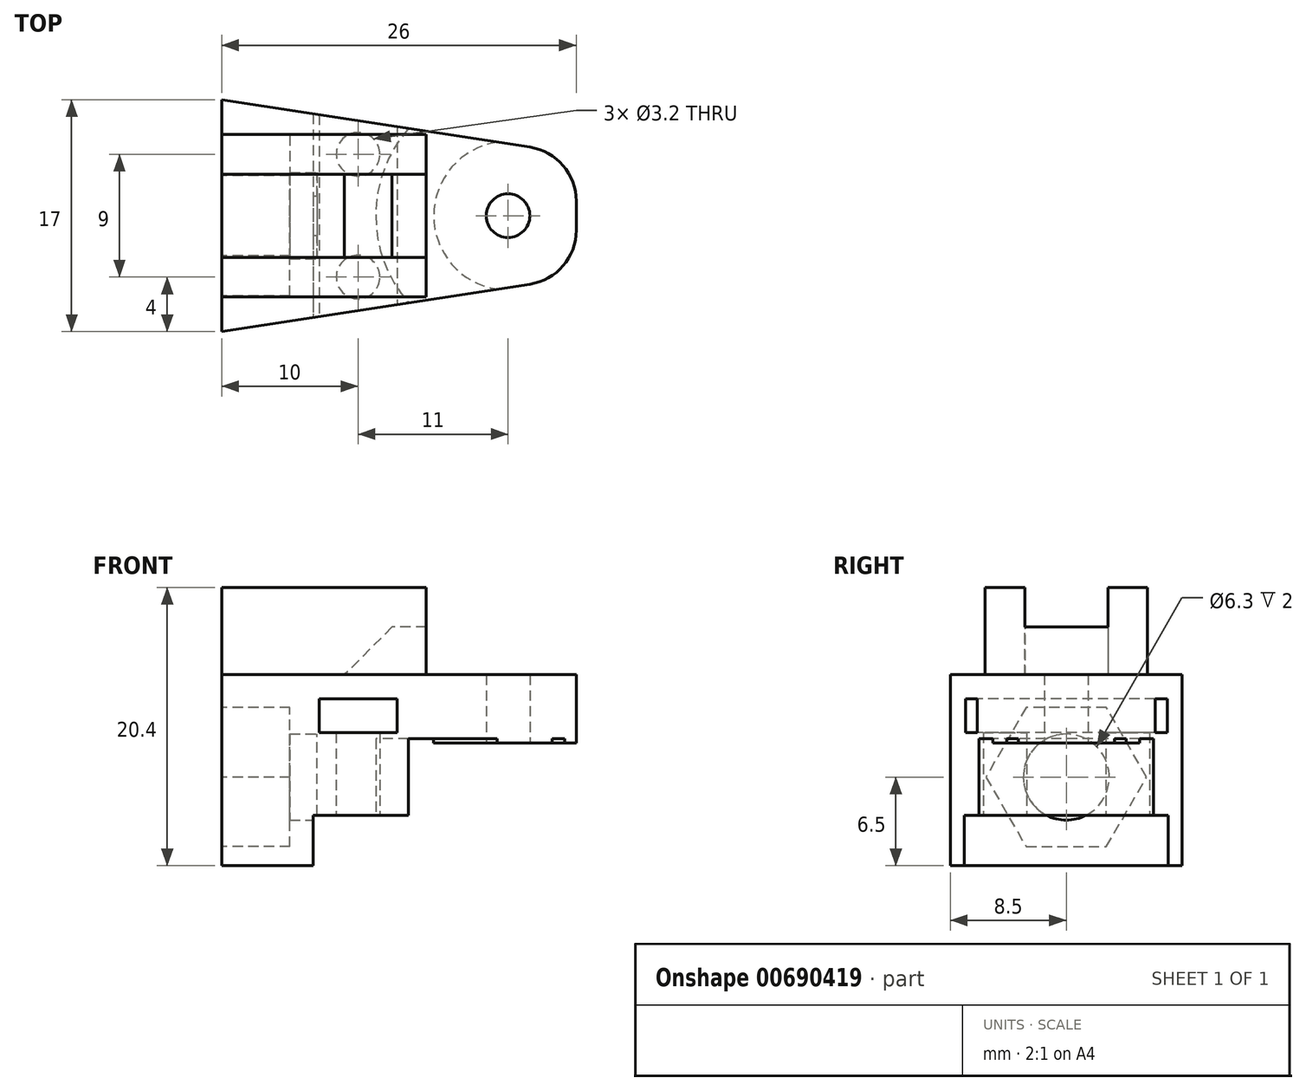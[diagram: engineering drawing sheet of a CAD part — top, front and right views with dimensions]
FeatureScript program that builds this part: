
annotation { "Feature Type Name" : "Feature", "Feature Type Description" : "" }
export const myFeature = defineFeature(function(context is Context, id is Id, definition is map)
    precondition{}
    {
        {
            var Q0;
            Q0=qCreatedBy(makeId("Top.planeOp"),FACE);
            var sketch = newSketch(context, id + "F0", { "sketchPlane" : qUnion([Q0])});
            skLineSegment(sketch, "E0.bottom", {"start": v(1.6, -5.02) * mm, "end": v(-21, -8.5) * mm});
            skLineSegment(sketch, "E0.top", {"start": v(1.6, 5.02) * mm, "end": v(-21, 8.5) * mm});
            skLineSegment(sketch, "E0.left", {"start": v(5, -1.07) * mm, "end": v(5, 1.07) * mm});
            skLineSegment(sketch, "E0.right", {"start": v(-21, -8.5) * mm, "end": v(-21, 8.5) * mm});
            skLineSegment(sketch, "E1", {"start": v(5, 0) * mm, "end": v(-21, 0) * mm, "construction": true});
            skPoint(sketch, "E2.visualSharp", {"position": v(5, -4.5) * mm});
            skArc(sketch, "E2.filletArc", {"start": v(1.6, -5.02) * mm, "mid": v(4.04, -3.67) * mm, "end": v(5, -1.07) * mm});
            skPoint(sketch, "E3.visualSharp", {"position": v(5, 4.5) * mm});
            skArc(sketch, "E3.filletArc", {"start": v(5, 1.07) * mm, "mid": v(4.04, 3.67) * mm, "end": v(1.6, 5.02) * mm});
            skSolve(sketch);
        }
        {
            var Q0;
            Q0=qSketchRegion(id+"F0",true);
            extrude(context, id + "F1", {"entities" : qUnion([Q0]), "depth" : 8 * mm, "offsetDistance" : 25 * mm, "hasSecondDirection" : true, "secondDirectionOppositeDirection" : true, "secondDirectionDepth" : 6 * mm});
        }
        {
            var Q0;
            Q0=qCreatedBy(makeId("Top.planeOp"),FACE);
            var sketch = newSketch(context, id + "F2", { "sketchPlane" : qUnion([Q0])});
            skCircle(sketch, "E4", {"center": v(0, 0) * mm, "radius": 8.3 * mm});
            skCircle(sketch, "E5", {"center": v(0, 0) * mm, "radius": 2.95 * mm});
            skSolve(sketch);
        }
        {
            var Q0;
            Q0=qSketchRegion(id+"F2",true);
            extrude(context, id + "F3", {"entities" : qUnion([Q0]), "operationType" : NewBodyOperationType.REMOVE, "oppositeDirection" : true, "depth" : 3 * mm, "offsetDistance" : 25 * mm, "hasSecondDirection" : true, "secondDirectionOppositeDirection" : false, "secondDirectionDepth" : 3 * mm});
        }
        {
            var Q0;
            Q0=qCreatedBy(makeId("Top.planeOp"),FACE);
            var sketch = newSketch(context, id + "F4", { "sketchPlane" : qUnion([Q0])});
            skArc(sketch, "E6", {"start": v(5, 2.17) * mm, "mid": v(-5.45, 0) * mm, "end": v(5, -2.17) * mm});
            skArc(sketch, "E7", {"start": v(5, 8.31) * mm, "mid": v(-9.7, 0) * mm, "end": v(5, -8.31) * mm});
            skLineSegment(sketch, "E8", {"start": v(5, 8.31) * mm, "end": v(5, 2.17) * mm});
            skLineSegment(sketch, "E9.trimOffspring", {"start": v(5, -2.17) * mm, "end": v(5, -8.31) * mm});
            skSolve(sketch);
        }
        {
            var Q0;
            Q0=qSketchRegion(id+"F4",true);
            extrude(context, id + "F5", {"entities" : qUnion([Q0]), "operationType" : NewBodyOperationType.REMOVE, "depth" : 3.3 * mm, "offsetDistance" : 25 * mm, "hasSecondDirection" : true, "secondDirectionOppositeDirection" : true, "secondDirectionDepth" : 3.3 * mm});
        }
        {
            var Q0;
            Q0=qCreatedBy(makeId("Right.planeOp"),FACE);
            var sketch = newSketch(context, id + "F6", { "sketchPlane" : qUnion([Q0])});
            skPoint(sketch, "E10", {"position": v(0, 0) * mm});
            skCircle(sketch, "E11", {"center": v(0, 0.5) * mm, "radius": 3.15 * mm});
            skSolve(sketch);
        }
        {
            var Q0;
            Q0=qSketchRegion(id+"F6",true);
            extrude(context, id + "F7", {"entities" : qUnion([Q0]), "operationType" : NewBodyOperationType.REMOVE, "oppositeDirection" : true, "depth" : 40 * mm, "offsetDistance" : 25 * mm, "hasSecondDirection" : true, "secondDirectionOppositeDirection" : true, "secondDirectionDepth" : 14 * mm});
        }
        {
            var Q0;
            Q0=makeQuery(id+"F1.opExtrude","SWEPT_FACE",FACE,{"disambiguationData":[OSD([sQuery(id+"F0.wireOp",EDGE,"E0.right")])]});
            var sketch = newSketch(context, id + "F8", { "sketchPlane" : qUnion([Q0])});
            skCircle(sketch, "E12.cCircle", {"center": v(0, 0.5) * mm, "radius": 5.1 * mm, "construction": true});
            skLineSegment(sketch, "E12.0", {"start": v(-2.94, 5.6) * mm, "end": v(2.94, 5.6) * mm});
            skLineSegment(sketch, "E12.1", {"start": v(2.94, 5.6) * mm, "end": v(5.89, 0.5) * mm});
            skLineSegment(sketch, "E12.2", {"start": v(5.89, 0.5) * mm, "end": v(2.94, -4.6) * mm});
            skLineSegment(sketch, "E12.3", {"start": v(2.94, -4.6) * mm, "end": v(-2.94, -4.6) * mm});
            skLineSegment(sketch, "E12.4", {"start": v(-2.94, -4.6) * mm, "end": v(-5.89, 0.5) * mm});
            skLineSegment(sketch, "E12.5", {"start": v(-5.89, 0.5) * mm, "end": v(-2.94, 5.6) * mm});
            skSolve(sketch);
        }
        {
            var Q0;
            Q0=qSketchRegion(id+"F8",true);
            extrude(context, id + "F9", {"entities" : qUnion([Q0]), "operationType" : NewBodyOperationType.REMOVE, "oppositeDirection" : true, "depth" : 5 * mm, "offsetDistance" : 25 * mm});
        }
        {
            var Q0;
            Q0=makeQuery(id+"F1.opExtrude","CAP_FACE",FACE,{"disambiguationData":[OSD([sQuery(id+"F0.wireOp",EDGE,"E0.bottom"),sQuery(id+"F0.wireOp",EDGE,"E0.top"),sQuery(id+"F0.wireOp",EDGE,"E0.left"),sQuery(id+"F0.wireOp",EDGE,"E0.right"),sQuery(id+"F0.wireOp",EDGE,"E2.filletArc"),sQuery(id+"F0.wireOp",EDGE,"E3.filletArc")])],"isStart":false});
            var sketch = newSketch(context, id + "F10", { "sketchPlane" : qUnion([Q0])});
            skLineSegment(sketch, "E13.bottom", {"start": v(-6, 3.05) * mm, "end": v(-21, 3.05) * mm});
            skLineSegment(sketch, "E13.top", {"start": v(-6, 5.95) * mm, "end": v(-21, 5.95) * mm});
            skLineSegment(sketch, "E13.left", {"start": v(-6, 3.05) * mm, "end": v(-6, 5.95) * mm});
            skLineSegment(sketch, "E13.right", {"start": v(-21, 3.05) * mm, "end": v(-21, 5.95) * mm});
            skPoint(sketch, "E13.middle", {"position": v(-13.5, 4.5) * mm});
            skLineSegment(sketch, "E14.MirrorCS", {"start": v(-6, -3.05) * mm, "end": v(-21, -3.05) * mm});
            skPoint(sketch, "E15.MirrorP", {"position": v(-13.5, -4.5) * mm});
            skLineSegment(sketch, "E16.MirrorCS", {"start": v(-6, -3.05) * mm, "end": v(-6, -5.95) * mm});
            skLineSegment(sketch, "E17.MirrorCS", {"start": v(-21, -3.05) * mm, "end": v(-21, -5.95) * mm});
            skLineSegment(sketch, "E18.MirrorCS", {"start": v(-6, -5.95) * mm, "end": v(-21, -5.95) * mm});
            skSolve(sketch);
        }
        {
            var Q0;
            Q0=qSketchRegion(id+"F10",true);
            extrude(context, id + "F11", {"entities" : qUnion([Q0]), "operationType" : NewBodyOperationType.ADD, "depth" : 6.4 * mm, "offsetDistance" : 25 * mm});
        }
        {
            var Q0;
            {var subQ3=sQuery(id+"F0.wireOp",EDGE,"E3.filletArc");var subQ4=sQuery(id+"F0.wireOp",EDGE,"E2.filletArc");var subQ5=sQuery(id+"F0.wireOp",EDGE,"E0.right");var subQ6=sQuery(id+"F0.wireOp",EDGE,"E0.left");var subQ7=sQuery(id+"F0.wireOp",EDGE,"E0.top");var subQ8=sQuery(id+"F0.wireOp",EDGE,"E0.bottom");var subQ9=makeQuery(id+"F1.opExtrude","CAP_FACE",FACE,{"disambiguationData":[OSD([subQ8,subQ7,subQ6,subQ5,subQ4,subQ3])],"isStart":false});Q0=makeQuery(id+"F11.boolean.opBoolean","SPLIT",FACE,{"disambiguationData":[TD([makeQuery(id+"F1.opExtrude","SWEPT_FACE",FACE,{"disambiguationData":[OSD([subQ6])]})])],"derivedFrom":subQ9});}
            var sketch = newSketch(context, id + "F12", { "sketchPlane" : qUnion([Q0])});
            skLineSegment(sketch, "E19.bottom", {"start": v(-6, -3.25) * mm, "end": v(-7, -3.25) * mm});
            skLineSegment(sketch, "E19.top", {"start": v(-6, 3.25) * mm, "end": v(-7, 3.25) * mm});
            skLineSegment(sketch, "E19.left", {"start": v(-6, -3.25) * mm, "end": v(-6, 3.25) * mm});
            skLineSegment(sketch, "E19.right", {"start": v(-7, -3.25) * mm, "end": v(-7, 3.25) * mm});
            skPoint(sketch, "E19.middle", {"position": v(-6.5, 0) * mm});
            skSolve(sketch);
        }
        {
            var Q0;
            Q0=qSketchRegion(id+"F12",true);
            extrude(context, id + "F13", {"entities" : qUnion([Q0]), "operationType" : NewBodyOperationType.ADD, "depth" : 3.5 * mm, "offsetDistance" : 25 * mm});
        }
        {
            var Q0;
            Q0=makeQuery(id+"F13.opExtrude","CAP_EDGE",EDGE,{"disambiguationData":[OSD([sQuery(id+"F12.wireOp",EDGE,"E19.right")])],"isStart":true});
            chamfer(context, id + "F14", {"entities" : qUnion([Q0]), "width" : 5 * mm, "tangentPropagation" : true});
        }
        {
            var Q0;
            Q0=makeQuery(id+"F1.opExtrude","CAP_FACE",FACE,{"disambiguationData":[OSD([sQuery(id+"F0.wireOp",EDGE,"E0.bottom"),sQuery(id+"F0.wireOp",EDGE,"E0.top"),sQuery(id+"F0.wireOp",EDGE,"E0.left"),sQuery(id+"F0.wireOp",EDGE,"E0.right"),sQuery(id+"F0.wireOp",EDGE,"E2.filletArc"),sQuery(id+"F0.wireOp",EDGE,"E3.filletArc")])],"isStart":true});
            var sketch = newSketch(context, id + "F15", { "sketchPlane" : qUnion([Q0])});
            skPoint(sketch, "E20", {"position": v(-11, 4.5) * mm});
            skPoint(sketch, "E21", {"position": v(-11, -4.5) * mm});
            skLineSegment(sketch, "E22", {"start": v(-11, 4.5) * mm, "end": v(-11, -4.5) * mm});
            skPoint(sketch, "E23", {"position": v(-11, 0) * mm});
            skSolve(sketch);
        }
        {
            var Q0;
            Q0=sQuery(id+"F15.wireOp",VERTEX,"E21");
            var Q1;
            Q1=sQuery(id+"F15.wireOp",VERTEX,"E20");
            var Q2;
            Q2=makeQuery(id+"F1.opExtrude","SWEPT_BODY",BODY,{"disambiguationData":[OSD([sQuery(id+"F0.wireOp",EDGE,"E0.bottom"),sQuery(id+"F0.wireOp",EDGE,"E0.top"),sQuery(id+"F0.wireOp",EDGE,"E0.left"),sQuery(id+"F0.wireOp",EDGE,"E0.right"),sQuery(id+"F0.wireOp",EDGE,"E2.filletArc"),sQuery(id+"F0.wireOp",EDGE,"E3.filletArc")])]});
            hole(context, id + "F16", {"style" : HoleStyle.C_BORE, "endStyle" : HoleEndStyle.BLIND, "holeDiameter" : 3.2 * mm, "cBoreDiameter" : 6.5 * mm, "cBoreDepth" : 2.5 * mm, "holeDepth" : 11 * mm, "isTappedThrough" : true, "tappedDepth" : 2.3 * mm, "tapClearance" : 3, "startFromSketch" : true, "locations" : qUnion([Q0, Q1]), "scope" : qUnion([Q2])});
        }
        {
            var Q0;
            Q0=makeQuery(id+"F1.opExtrude","CAP_FACE",FACE,{"disambiguationData":[OSD([sQuery(id+"F0.wireOp",EDGE,"E0.bottom"),sQuery(id+"F0.wireOp",EDGE,"E0.top"),sQuery(id+"F0.wireOp",EDGE,"E0.left"),sQuery(id+"F0.wireOp",EDGE,"E0.right"),sQuery(id+"F0.wireOp",EDGE,"E2.filletArc"),sQuery(id+"F0.wireOp",EDGE,"E3.filletArc")])],"isStart":true});
            var sketch = newSketch(context, id + "F17", { "sketchPlane" : qUnion([Q0])});
            skPoint(sketch, "E24", {"position": v(0, 0) * mm});
            skSolve(sketch);
        }
        {
            var Q0;
            Q0=sQuery(id+"F17.wireOp",VERTEX,"E24");
            var Q1;
            Q1=makeQuery(id+"F1.opExtrude","SWEPT_BODY",BODY,{"disambiguationData":[OSD([sQuery(id+"F0.wireOp",EDGE,"E0.bottom"),sQuery(id+"F0.wireOp",EDGE,"E0.top"),sQuery(id+"F0.wireOp",EDGE,"E0.left"),sQuery(id+"F0.wireOp",EDGE,"E0.right"),sQuery(id+"F0.wireOp",EDGE,"E2.filletArc"),sQuery(id+"F0.wireOp",EDGE,"E3.filletArc")])]});
            hole(context, id + "F18", {"style" : HoleStyle.C_BORE, "endStyle" : HoleEndStyle.THROUGH, "holeDiameter" : 3.2 * mm, "cBoreDiameter" : 6.2 * mm, "cBoreDepth" : 2.6 * mm, "isTappedThrough" : true, "tappedDepth" : 2.3 * mm, "tapClearance" : 3, "startFromSketch" : true, "locations" : qUnion([Q0]), "scope" : qUnion([Q1])});
        }
        {
            var Q0;
            Q0=qCreatedBy(makeId("Front.planeOp"),FACE);
            var sketch = newSketch(context, id + "F19", { "sketchPlane" : qUnion([Q0])});
            skLineSegment(sketch, "E25", {"start": v(10, 3) * mm, "end": v(-6.1, 3) * mm});
            skLineSegment(sketch, "E26", {"start": v(-6.1, 3) * mm, "end": v(-6.1, -2.3) * mm});
            skLineSegment(sketch, "E27", {"start": v(-6.1, -2.3) * mm, "end": v(-14.3, -2.3) * mm});
            skLineSegment(sketch, "E28", {"start": v(-14.3, -2.3) * mm, "end": v(-14.3, -7.58) * mm});
            skLineSegment(sketch, "E29", {"start": v(-14.3, -7.58) * mm, "end": v(9.83, -7.58) * mm});
            skLineSegment(sketch, "E30", {"start": v(9.83, -7.58) * mm, "end": v(10, 3) * mm});
            skSolve(sketch);
        }
        {
            var Q0;
            Q0=qSketchRegion(id+"F19",true);
            extrude(context, id + "F20", {"entities" : qUnion([Q0]), "operationType" : NewBodyOperationType.REMOVE, "oppositeDirection" : true, "depth" : 25 * mm, "offsetDistance" : 25 * mm, "hasSecondDirection" : true, "secondDirectionOppositeDirection" : false, "secondDirectionDepth" : 25 * mm});
        }
        {
            var Q0;
            Q0=qCreatedBy(makeId("Front.planeOp"),FACE);
            var sketch = newSketch(context, id + "F21", { "sketchPlane" : qUnion([Q0])});
            skLineSegment(sketch, "E31.bottom", {"start": v(-8.15, 3.75) * mm, "end": v(-13.85, 3.75) * mm});
            skLineSegment(sketch, "E31.top", {"start": v(-8.15, 6.25) * mm, "end": v(-13.85, 6.25) * mm});
            skLineSegment(sketch, "E31.left", {"start": v(-8.15, 3.75) * mm, "end": v(-8.15, 6.25) * mm});
            skLineSegment(sketch, "E31.right", {"start": v(-13.85, 3.75) * mm, "end": v(-13.85, 6.25) * mm});
            skPoint(sketch, "E31.middle", {"position": v(-11, 5) * mm});
            skSolve(sketch);
        }
        {
            var Q0;
            Q0=qSketchRegion(id+"F21",true);
            extrude(context, id + "F22", {"entities" : qUnion([Q0]), "operationType" : NewBodyOperationType.REMOVE, "oppositeDirection" : true, "depth" : 25 * mm, "offsetDistance" : 25 * mm, "hasSecondDirection" : true, "secondDirectionOppositeDirection" : false, "secondDirectionDepth" : 25 * mm});
        }
    });
